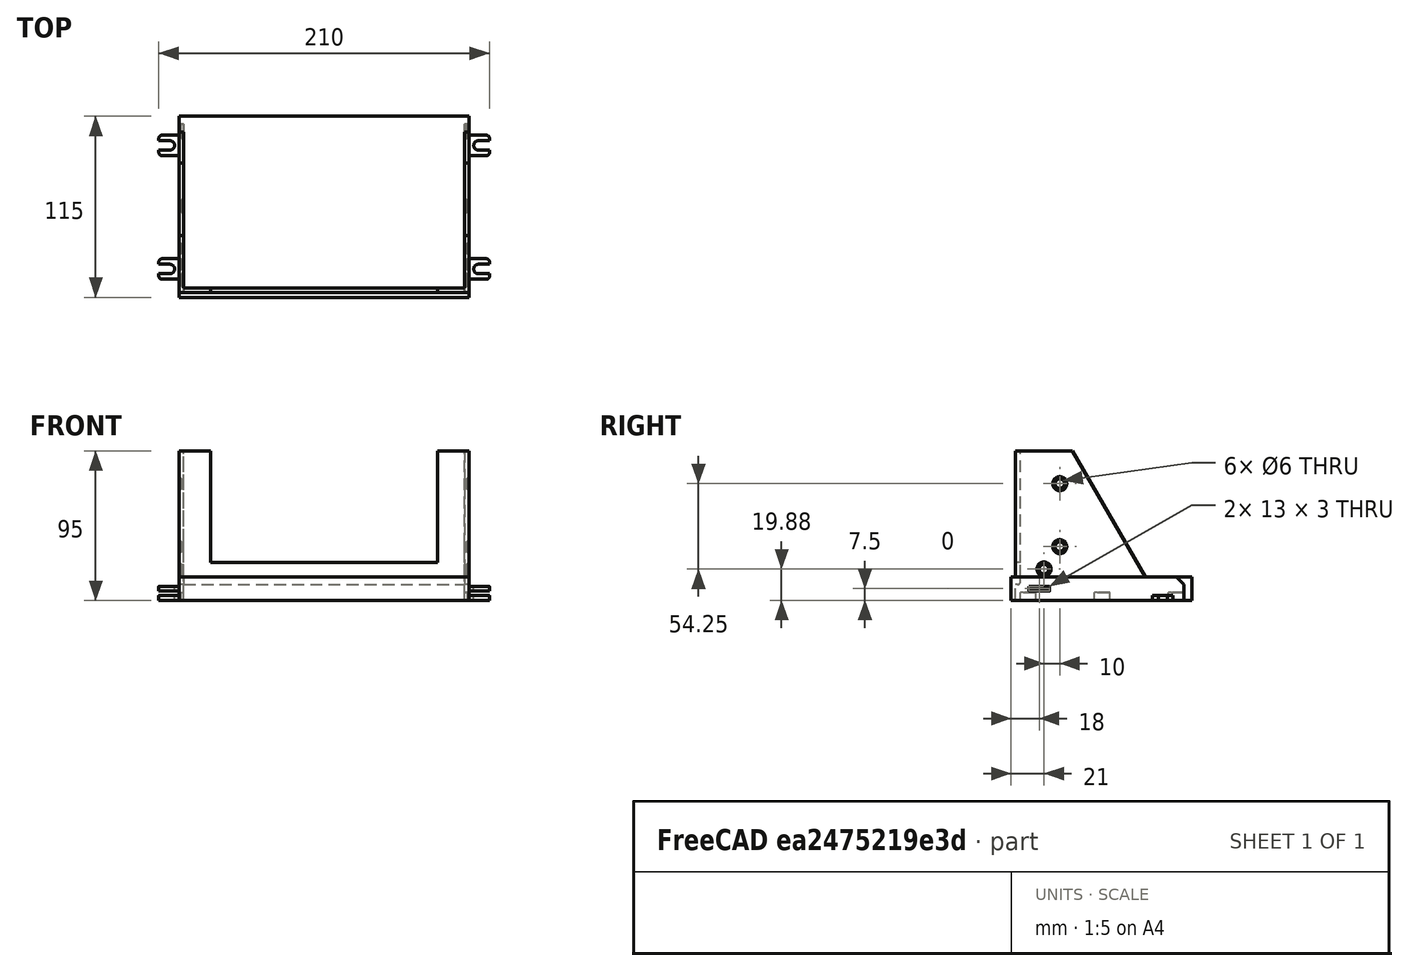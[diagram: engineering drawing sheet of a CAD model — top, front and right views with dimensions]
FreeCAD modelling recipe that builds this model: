
FCSTD DOCUMENT  (FreeCAD 0.19R24291 (Git))
Label: carrier-atoto-s8
License: All rights reserved
LicenseURL: http://en.wikipedia.org/wiki/All_rights_reserved
objects: Part::Box×19, Part::Cut×10, Part::MultiFuse×8, Part::Cylinder×7, TechDraw::DrawViewDimension×7, PartDesign::Fillet×4, TechDraw::DrawProjGroupItem×4, Part::Fillet×3, Part::Fuse×2, Part::Compound×2, PartDesign::Chamfer×1, Part::Chamfer×1, App::Link×1, TechDraw::DrawSVGTemplate×1, TechDraw::DrawProjGroup×1, TechDraw::DrawPage×1
note: 62 computed .brp shape members not serialized (recipe doc carries the construction recipe); baked Part::Feature solids carry a one-line shape summary decoded from their .brp

FEATURE [Part::Box] Box  label="Cube"
  AttacherType = Attacher::AttachEngine3D
  Height = 15
  Length = 184
  Placement = pos=(1,0,5) rot=(0,0,1;0rad)
  Width = 115
FEATURE [Part::Cylinder] Cylinder
  Angle = 360
  AttacherType = Attacher::AttachEngine3D
  Height = 10
  Placement = pos=(7,6.5,0) rot=(0,0,1;0rad)
  Radius = 3
FEATURE [Part::Box] Box003  label="Cube003"
  AttacherType = Attacher::AttachEngine3D
  Height = 10
  Length = 7
  Placement = pos=(0,3.5,0) rot=(0,0,1;0rad)
  Width = 6
FEATURE [PartDesign::Fillet] Fillet001
  Radius = 2
  SupportTransform = false
FEATURE [Part::MultiFuse] Fusion
  Shapes = -> [Box003,Cylinder]
FEATURE [Part::Cut] Cut001  label="Mounting Point 001"
  Base = -> Fillet001
  Placement = pos=(-12,11.5,11) rot=(0,0,1;0rad)
  Tool = -> Fusion
FEATURE [Part::Cylinder] Cylinder001
  Angle = 360
  AttacherType = Attacher::AttachEngine3D
  Height = 10
  Placement = pos=(7,6.5,0) rot=(0,0,1;0rad)
  Radius = 3
FEATURE [Part::Box] Box005  label="Cube005"
  AttacherType = Attacher::AttachEngine3D
  Height = 10
  Length = 7
  Placement = pos=(0,3.5,0) rot=(0,0,1;0rad)
  Width = 6
FEATURE [PartDesign::Fillet] Fillet003
  Radius = 2
  SupportTransform = false
FEATURE [Part::MultiFuse] Fusion001
  Shapes = -> [Box005,Cylinder001]
FEATURE [Part::Cut] Cut002  label="Mounting Point 002"
  Base = -> Fillet003
  Placement = pos=(-12,90,5) rot=(0,0,1;0rad)
  Tool = -> Fusion001
FEATURE [Part::Cylinder] Cylinder002
  Angle = 360
  AttacherType = Attacher::AttachEngine3D
  Height = 10
  Placement = pos=(7,6.5,0) rot=(0,0,1;0rad)
  Radius = 3
FEATURE [Part::Box] Box007  label="Cube007"
  AttacherType = Attacher::AttachEngine3D
  Height = 10
  Length = 7
  Placement = pos=(0,3.5,0) rot=(0,0,1;0rad)
  Width = 6
FEATURE [PartDesign::Fillet] Fillet005
  Radius = 2
  SupportTransform = false
FEATURE [Part::MultiFuse] Fusion002
  Shapes = -> [Box007,Cylinder002]
FEATURE [Part::Cut] Cut003  label="Mounting Point 003"
  Base = -> Fillet005
  Placement = pos=(198,24.5,11) rot=(0,0,1;3.14159rad)
  Tool = -> Fusion002
FEATURE [Part::Cylinder] Cylinder003
  Angle = 360
  AttacherType = Attacher::AttachEngine3D
  Height = 10
  Placement = pos=(7,6.5,0) rot=(0,0,1;0rad)
  Radius = 3
FEATURE [Part::Box] Box009  label="Cube009"
  AttacherType = Attacher::AttachEngine3D
  Height = 10
  Length = 7
  Placement = pos=(0,3.5,0) rot=(0,0,1;0rad)
  Width = 6
FEATURE [PartDesign::Fillet] Fillet007
  Radius = 2
  SupportTransform = false
FEATURE [Part::MultiFuse] Fusion003
  Shapes = -> [Box009,Cylinder003]
FEATURE [Part::Cut] Cut004  label="Mounting Point 004"
  Base = -> Fillet007
  Placement = pos=(198,103,5) rot=(0,0,1;3.14159rad)
  Tool = -> Fusion003
FEATURE [Part::Box] Box010  label="Cube010"
  AttacherType = Attacher::AttachEngine3D
  Height = 80
  Length = 2.75
  Placement = pos=(0,10,30) rot=(0,0,1;0rad)
  Width = 80
FEATURE [Part::Box] Box011  label="Cube011"
  AttacherType = Attacher::AttachEngine3D
  Height = 80
  Length = 4
  Placement = pos=(0,38,119) rot=(-1,0,0;1.0472rad)
  Width = 150
FEATURE [Part::Cut] Cut005
  Base = -> Box010
  Tool = -> Box011
FEATURE [Part::Box] Box012  label="Cube012"
  AttacherType = Attacher::AttachEngine3D
  Height = 80
  Length = 20
  Placement = pos=(0,7,30) rot=(0,0,1;0rad)
  Width = 3
FEATURE [Part::Fuse] Fusion005  label="Left Support"
  Base = -> Cut005
  Placement = pos=(0,-3,0) rot=(0,0,1;0rad)
  Tool = -> Box012
FEATURE [Part::Box] Box013  label="Cube013"
  AttacherType = Attacher::AttachEngine3D
  Height = 80
  Length = 2.75
  Placement = pos=(-2.75,10,30) rot=(0,0,1;0rad)
  Width = 80
FEATURE [Part::Box] Box014  label="Cube014"
  AttacherType = Attacher::AttachEngine3D
  Height = 80
  Length = 4
  Placement = pos=(-2.75,38,119) rot=(-1,0,0;1.0472rad)
  Width = 150
FEATURE [Part::Cut] Cut006
  Base = -> Box013
  Tool = -> Box014
FEATURE [Part::Box] Box015  label="Cube015"
  AttacherType = Attacher::AttachEngine3D
  Height = 80
  Length = 20
  Placement = pos=(-20,7,30) rot=(0,0,1;0rad)
  Width = 3
FEATURE [Part::Fuse] Fusion006  label="Right Support"
  Base = -> Cut006
  Placement = pos=(184,-3,0) rot=(0,0,1;0rad)
  Tool = -> Box015
FEATURE [Part::Box] Box016  label="Cross Brace"
  AttacherType = Attacher::AttachEngine3D
  Height = 14
  Length = 184
  Placement = pos=(0,4,25) rot=(0,0,1;0rad)
  Width = 3
FEATURE [Part::MultiFuse] Fusion008  label="Carrier"
  Placement = pos=(1,-1,0) rot=(0,0,1;0rad)
  Shapes = -> [Fusion005,Fusion006,Box016]
FEATURE [PartDesign::Chamfer] Chamfer  label="Carrier Frame"
  Angle = 45
  ChamferType = 0
  FlipDirection = false
  Size = 10
  Size2 = 1
  SupportTransform = false
FEATURE [Part::MultiFuse] Fusion012  label="Carrier (No Mounts)"
  Shapes = -> [Chamfer,Fusion008]
FEATURE [Part::Cylinder] Cylinder004
  Angle = 360
  AttacherType = Attacher::AttachEngine3D
  Height = 200
  Placement = pos=(0,0,0) rot=(0,1,0;1.5708rad)
  Radius = 3
FEATURE [Part::Cylinder] Cylinder005
  Angle = 360
  AttacherType = Attacher::AttachEngine3D
  Height = 200
  Placement = pos=(0,0,40) rot=(0,1,0;1.5708rad)
  Radius = 3
FEATURE [Part::Cylinder] Cylinder006
  Angle = 360
  AttacherType = Attacher::AttachEngine3D
  Height = 200
  Placement = pos=(0,-10,-14.25) rot=(0,1,0;1.5708rad)
  Radius = 3
FEATURE [Part::MultiFuse] Fusion013  label="Mounting Points"
  Placement = pos=(-5,31,49.13) rot=(0,0,1;0rad)
  Shapes = -> [Cylinder004,Cylinder005,Cylinder006]
FEATURE [Part::Cut] Cut011
  Base = -> Fusion012
  Tool = -> Fusion013
FEATURE [Part::Chamfer] Chamfer005  label="Carrier (Unmodified)"
  Base = -> Cut011
  Edges = 6 edges r=1.5: [Edge86,Edge87,Edge88,Edge199,Edge200,Edge201]
FEATURE [Part::Box] Box020  label="Cube017"
  AttacherType = Attacher::AttachEngine3D
  Height = 20
  Length = 200
  Placement = pos=(0,110,10) rot=(0,0,1;0rad)
  Width = 10
FEATURE [Part::Cut] Cut
  Base = -> Chamfer005
  Tool = -> Box020
FEATURE [Part::Box] Box021  label="Cube018"
  AttacherType = Attacher::AttachEngine3D
  Height = 10
  Length = 10
  Width = 10
FEATURE [Part::Box] Box022  label="Cube019"
  AttacherType = Attacher::AttachEngine3D
  Height = 10
  Length = 10
  Placement = pos=(0,47,0) rot=(0,0,1;0rad)
  Width = 10
FEATURE [Part::Box] Box023  label="Cube020"
  AttacherType = Attacher::AttachEngine3D
  Height = 10
  Length = 10
  Placement = pos=(0,94,0) rot=(0,0,1;0rad)
  Width = 20
FEATURE [Part::Compound] Compound
  Links = -> [Box023,Box022,Box021]
  Placement = pos=(0,6,0) rot=(0,0,1;0rad)
FEATURE [Part::Box] Box024  label="Cube021"
  AttacherType = Attacher::AttachEngine3D
  Height = 10
  Length = 10
  Placement = pos=(0,47,0) rot=(0,0,1;0rad)
  Width = 10
FEATURE [Part::Box] Box025  label="Cube022"
  AttacherType = Attacher::AttachEngine3D
  Height = 10
  Length = 10
  Placement = pos=(0,94,0) rot=(0,0,1;0rad)
  Width = 20
FEATURE [Part::Box] Box026  label="Cube023"
  AttacherType = Attacher::AttachEngine3D
  Height = 10
  Length = 10
  Width = 10
FEATURE [Part::Compound] Compound001
  Links = -> [Box025,Box024,Box026]
  Placement = pos=(0,6,0) rot=(0,0,1;0rad)
FEATURE [Part::Fillet] Fillet
  Base = -> Compound
  Edges = 6 edges r=2: [Edge1,Edge3,Edge13,Edge15,Edge25,Edge27]
  Placement = pos=(2.25,0,10) rot=(0,0,1;0rad)
FEATURE [Part::Fillet] Fillet010
  Base = -> Cut
  Edges = 1 edges r=2: [Edge184]
FEATURE [Part::Cut] Cut012
  Base = -> Fillet010
  Tool = -> Fillet
FEATURE [Part::Fillet] Fillet011
  Base = -> Compound001
  Edges = 6 edges r=2: [Edge5,Edge7,Edge17,Edge19,Edge29,Edge31]
  Placement = pos=(173.75,0,10) rot=(0,0,1;0rad)
FEATURE [Part::Cut] Cut013  label="Carrier (Complete)"
  Base = -> Cut012
  Tool = -> Fillet011
FEATURE [Part::MultiFuse] Fusion009  label="Mounting Frame (Do Not Delete)"
  Placement = pos=(0,0,10) rot=(0,0,1;0rad)
  Shapes = -> [Box,Cut001,Cut002,Cut003,Cut004]
FEATURE [App::Link] Link  label="Mount Points (Edit as needed) "
  LinkedObject = -> Fusion013
FEATURE [TechDraw::DrawSVGTemplate] Template
  EditableTexts = AUTHOR_NAME=FLOYD DIEBEL; DN=DN; DRAWING_TITLE=MIATA NA HEAD UNIT CARRIER FOR ATOTO S8; FC-DATE=DD/MM/YYYY; FC-REV=REV A; FC-SC=SCALE; FC-SH=X / Y; FC-SI=A2; FreeCAD_DRAWING=FreeCAD DRAWING; PN=PN
  Height = 420
  Orientation = 1
  Width = 594
FEATURE [TechDraw::DrawProjGroupItem] ProjItem  label="Front"
  CoarseView = false
  Direction = (0,0,-1)
  Focus = 100
  HardHidden = false
  IsoCount = 0
  IsoHidden = false
  IsoVisible = false
  LockPosition = true
  Perspective = false
  Rotation = 0
  RotationVector = (1,0,0)
  ScaleType = 2
  SeamHidden = false
  SeamVisible = true
  SmoothHidden = false
  SmoothVisible = true
  Source = -> [Cut013]
  Type = 0
  X = 0
  XDirection = (1,0,0)
  Y = 0
FEATURE [TechDraw::DrawProjGroupItem] ProjItem001  label="Left"
  CoarseView = false
  Direction = (-1,0,-1e-16)
  Focus = 100
  HardHidden = false
  IsoCount = 0
  IsoHidden = false
  IsoVisible = false
  LockPosition = false
  Perspective = false
  Rotation = 0
  RotationVector = (1,0,0)
  ScaleType = 2
  SeamHidden = false
  SeamVisible = true
  SmoothHidden = false
  SmoothVisible = true
  Source = -> [Cut013]
  Type = 1
  X = 167.5
  XDirection = (1e-16,0,-1)
  Y = 0
FEATURE [TechDraw::DrawProjGroupItem] ProjItem002  label="Bottom"
  CoarseView = false
  Direction = (0,1,0)
  Focus = 100
  HardHidden = false
  IsoCount = 0
  IsoHidden = false
  IsoVisible = false
  LockPosition = false
  Perspective = false
  Rotation = 0
  RotationVector = (1,0,0)
  ScaleType = 2
  SeamHidden = false
  SeamVisible = true
  SmoothHidden = false
  SmoothVisible = true
  Source = -> [Cut013]
  Type = 5
  X = 0
  XDirection = (1,0,0)
  Y = 167.5
FEATURE [TechDraw::DrawProjGroupItem] ProjItem003  label="FrontTopRight"
  CoarseView = false
  Direction = (0.57735,-0.57735,-0.57735)
  Focus = 100
  HardHidden = false
  IsoCount = 0
  IsoHidden = false
  IsoVisible = false
  LockPosition = false
  Perspective = false
  Rotation = 0
  RotationVector = (1,0,0)
  ScaleType = 2
  SeamHidden = false
  SeamVisible = true
  SmoothHidden = false
  SmoothVisible = true
  Source = -> [Cut013]
  Type = 7
  X = 295.545
  XDirection = (0.707107,0,0.707107)
  Y = 179.435
FEATURE [TechDraw::DrawProjGroup] ProjGroup
  Anchor = -> ProjItem
  AutoDistribute = true
  LockPosition = false
  ProjectionType = 0
  Rotation = 0
  ScaleType = 0
  Source = -> [Cut013]
  Views = -> [ProjItem,ProjItem001,ProjItem002,ProjItem003]
  X = 150.213
  Y = 116.99
  spacingX = 15
  spacingY = 15
FEATURE [TechDraw::DrawViewDimension] Dimension001
  Arbitrary = false
  ArbitraryTolerances = false
  EqualTolerance = true
  FormatSpec = %.2f
  FormatSpecOverTolerance = %+.2f
  FormatSpecUnderTolerance = %+.2f
  Inverted = false
  LockPosition = false
  MeasureType = 1
  OverTolerance = 0
  References2D = -> [ProjItem001]
  Rotation = 0
  ScaleType = 0
  TheoreticalExact = false
  Type = 2
  UnderTolerance = 0
  X = -58.7955
  Y = 34.0644
FEATURE [TechDraw::DrawViewDimension] Dimension002
  Arbitrary = false
  ArbitraryTolerances = false
  EqualTolerance = true
  FormatSpec = %.2f
  FormatSpecOverTolerance = %+.2f
  FormatSpecUnderTolerance = %+.2f
  Inverted = false
  LockPosition = false
  MeasureType = 1
  OverTolerance = 0
  References2D = -> [ProjItem001]
  Rotation = 0
  ScaleType = 0
  TheoreticalExact = false
  Type = 1
  UnderTolerance = 0
  X = -2.21507
  Y = 67.455
FEATURE [TechDraw::DrawViewDimension] Dimension003
  Arbitrary = false
  ArbitraryTolerances = false
  EqualTolerance = true
  FormatSpec = ⌀%.2f
  FormatSpecOverTolerance = %+.2f
  FormatSpecUnderTolerance = %+.2f
  Inverted = false
  LockPosition = false
  MeasureType = 1
  OverTolerance = 0
  References2D = -> [ProjItem001]
  Rotation = 0
  ScaleType = 0
  TheoreticalExact = false
  Type = 5
  UnderTolerance = 0
  X = 6.64522
  Y = 4.87316
FEATURE [TechDraw::DrawViewDimension] Dimension004
  Arbitrary = false
  ArbitraryTolerances = false
  EqualTolerance = true
  FormatSpec = ⌀%.2f
  FormatSpecOverTolerance = %+.2f
  FormatSpecUnderTolerance = %+.2f
  Inverted = false
  LockPosition = false
  MeasureType = 1
  OverTolerance = 0
  References2D = -> [ProjItem001]
  Rotation = 0
  ScaleType = 0
  TheoreticalExact = false
  Type = 5
  UnderTolerance = 0
  X = 11.5184
  Y = 14.1765
FEATURE [TechDraw::DrawViewDimension] Dimension005
  Arbitrary = false
  ArbitraryTolerances = false
  EqualTolerance = true
  FormatSpec = %.2f
  FormatSpecOverTolerance = %+.2f
  FormatSpecUnderTolerance = %+.2f
  Inverted = false
  LockPosition = false
  MeasureType = 1
  OverTolerance = 0
  References2D = -> [ProjItem002]
  Rotation = 0
  ScaleType = 0
  TheoreticalExact = false
  Type = 2
  UnderTolerance = 0
  X = 116.808
  Y = -4.5
FEATURE [TechDraw::DrawViewDimension] Dimension006
  Arbitrary = false
  ArbitraryTolerances = false
  EqualTolerance = true
  FormatSpec = %.2f
  FormatSpecOverTolerance = %+.2f
  FormatSpecUnderTolerance = %+.2f
  Inverted = false
  LockPosition = false
  MeasureType = 1
  OverTolerance = 0
  References2D = -> [ProjItem]
  Rotation = 0
  ScaleType = 0
  TheoreticalExact = false
  Type = 1
  UnderTolerance = 0
  X = 0.907509
  Y = 40.684
FEATURE [TechDraw::DrawViewDimension] Dimension
  Arbitrary = false
  ArbitraryTolerances = false
  EqualTolerance = true
  FormatSpec = %.2f
  FormatSpecOverTolerance = %+.2f
  FormatSpecUnderTolerance = %+.2f
  Inverted = false
  LockPosition = false
  MeasureType = 1
  OverTolerance = 0
  References2D = -> [ProjItem]
  Rotation = 0
  ScaleType = 0
  TheoreticalExact = false
  Type = 1
  UnderTolerance = 0
  X = -0.503157
  Y = 68.5852
FEATURE [TechDraw::DrawPage] Page
  KeepUpdated = true
  NextBalloonIndex = 1
  ProjectionType = 0
  Template = -> Template
  Views = -> [ProjGroup,Dimension001,Dimension002,Dimension003,Dimension004,Dimension005,Dimension006,Dimension]
